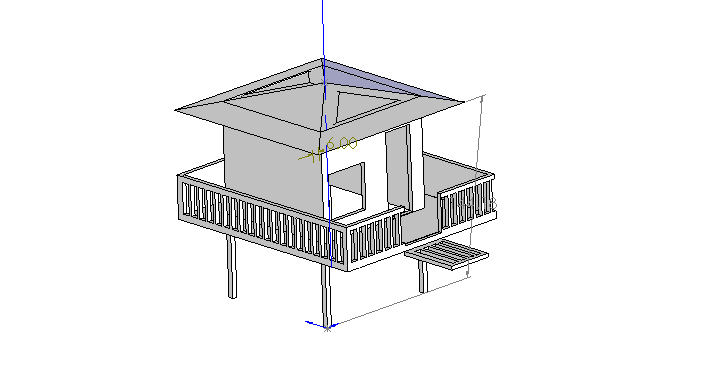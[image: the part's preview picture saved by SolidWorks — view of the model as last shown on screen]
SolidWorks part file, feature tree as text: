
SOLIDWORKS PART (.sldprt)
format: sldprt  version: not decoded by parser v0  size: 970,752 bytes
history: native  units: mm
features: sketch x16, cut_extrude x6, extrude x5, plane x5, shell x4 + 1 further entry (+10 scaffold rows collapsed)
feature tree (47):
  "Annotations"  RD2=152.4mm RD3=3662.246046mm
  scaffold x10  (default folders/planes/origin — collapsed)
  sketch  "Sketch1"  dims[c1.D1=101.6mm c1.D2=101.6mm c2.D1=101.6mm c2.D2=101.6mm c2.D3=90.0deg c2.D4=3048.0mm]
  extrude  "Extrude1"  Depth=1524mm
  sketch  "Sketch27"
  extrude  "Extrude3"  Depth=2540mm
  plane  "Plane1"
  plane  "Plane2"  Offset=1219.2mm
  sketch  "Sketch28"  dims[D1=1219.2mm D2=1219.2mm]
  plane  "Plane3"  Offset=1219.2mm
  sketch  "Sketch33"  dims[c1.D1=914.4mm c1.D2=914.4mm c1.D3=1574.8mm c2.D1=1219.2mm c2.D2=304.8mm c2.D3=304.8mm]
  cut_extrude  "Cut-Extrude19"  [1 undecoded]
  shell  "Shell6"  Thickness=88.9mm
  sketch  "Sketch34"  dims[c1.D1=609.6mm c1.D2=1219.2mm c1.D3=609.6mm c1.D4=609.6mm c2.D1=609.6mm c2.D2=609.6mm c2.D3=609.6mm c2.D4=1219.2mm c3.D1=609.6mm c3.D2=609.6mm c3.D3=609.6mm c3.D4=1219.2mm c4.D1=609.6mm]
  extrude  "Extrude4"  Depth=88.9mm
  sketch  "Sketch35"  dims[D1=88.9mm]
  extrude  "Extrude5"  Depth=762mm
  sketch  "Sketch36"  dims[D1=152.4mm D2=609.6mm D3=152.4mm]
  cut_extrude  "Cut-Extrude20"  Depth=127mm
  sketch  "Sketch39"  dims[D1=609.6mm D2=914.4mm D3=1676.4mm D4=914.4mm D5=457.2mm D6=101.6mm D7=152.4mm D8=304.8mm]
  cut_extrude  "Cut-Extrude22"  Depth=127mm
  sketch  "Sketch40"
  cut_extrude  "Cut-Extrude23"  [1 undecoded]
  sketch  "Sketch41"  dims[D1=152.4mm D2=609.6mm]
  cut_extrude  "Cut-Extrude24"  [1 undecoded]
  sketch  "Sketch42"
  sketch  "Sketch43"
  shell  "Surface-Plane3"  [1 undecoded]
  sketch  "Sketch44"  dims[c1.D1=~1104.197091mm c2.D1=90.0deg c3.D1=914.4mm c3.D2=457.2mm c3.D3=101.6mm]
  cut_extrude  "Cut-Extrude25"  Depth=127mm
  sketch  "Sketch45"  dims[D1=914.4mm D2=1219.2mm D3=914.4mm]
  extrude  "Extrude6"  Depth=76.2mm
  sketch  "Sketch46"  dims[D1=~181.818136mm]
  shell  "Surface-Plane4"  [1 undecoded]
  sketch  "Sketch47"
  shell  "Surface-Plane5"  [1 undecoded]
  plane  "Plane4"
  plane  "Plane5"
decode coverage: 20 of 31 modeling features carry decoded parameters; 1 rows unclassified (native names shown)
note: ~ marks probable driven/reference dimensions
note: 6 parameter values undecoded
summary: no parameter record found for 6 features
note: suppression state not decoded; provenance and decode notes live in map.json
